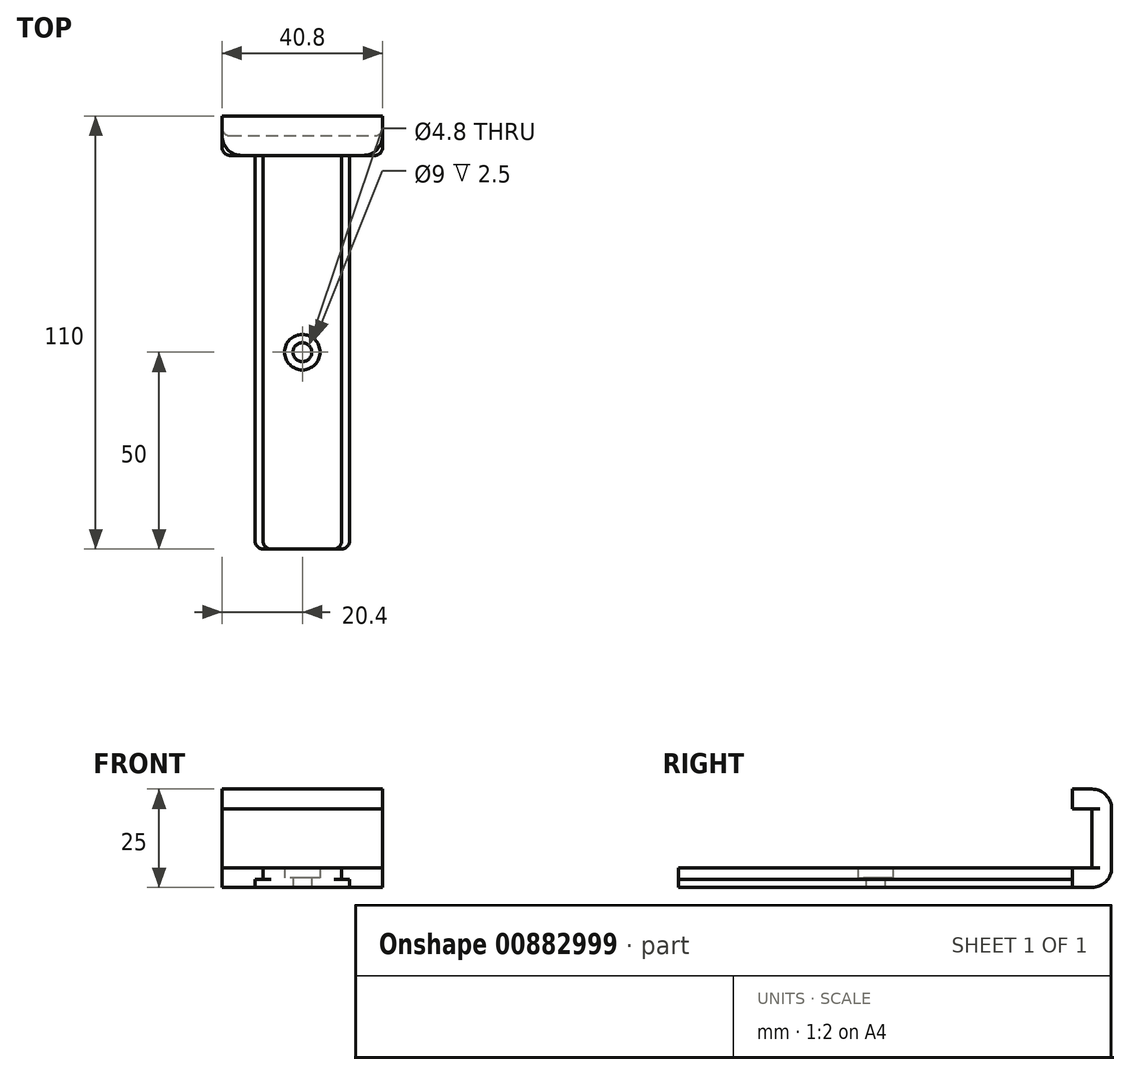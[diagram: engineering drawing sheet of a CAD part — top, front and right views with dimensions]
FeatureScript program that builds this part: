
annotation { "Feature Type Name" : "Feature", "Feature Type Description" : "" }
export const myFeature = defineFeature(function(context is Context, id is Id, definition is map)
    precondition{}
    {
        {
            var Q0;
            Q0=qCreatedBy(makeId("Top.planeOp"),FACE);
            var sketch = newSketch(context, id + "F0", { "sketchPlane" : qUnion([Q0])});
            skLineSegment(sketch, "E0.bottom", {"start": v(10, -50) * mm, "end": v(-10, -50) * mm});
            skLineSegment(sketch, "E0.top", {"start": v(10, 50) * mm, "end": v(-10, 50) * mm});
            skLineSegment(sketch, "E0.left", {"start": v(10, -50) * mm, "end": v(10, 50) * mm});
            skLineSegment(sketch, "E0.right", {"start": v(-10, -50) * mm, "end": v(-10, 50) * mm});
            skPoint(sketch, "E0.middle", {"position": v(0, 0) * mm});
            skLineSegment(sketch, "E1.bottom", {"start": v(-10, -50) * mm, "end": v(-12, -50) * mm});
            skLineSegment(sketch, "E1.top", {"start": v(-10, 50) * mm, "end": v(-12, 50) * mm});
            skLineSegment(sketch, "E1.right", {"start": v(-12, -50) * mm, "end": v(-12, 50) * mm});
            skLineSegment(sketch, "E2.bottom", {"start": v(10, 50) * mm, "end": v(12, 50) * mm});
            skLineSegment(sketch, "E2.top", {"start": v(10, -50) * mm, "end": v(12, -50) * mm});
            skLineSegment(sketch, "E2.left", {"start": v(10, 50) * mm, "end": v(10, -50) * mm});
            skLineSegment(sketch, "E2.right", {"start": v(12, 50) * mm, "end": v(12, -50) * mm});
            skLineSegment(sketch, "E3", {"start": v(0, 50) * mm, "end": v(20.4, 50) * mm});
            skLineSegment(sketch, "E4", {"start": v(20.4, 50) * mm, "end": v(20.4, 60) * mm});
            skLineSegment(sketch, "E5", {"start": v(20.4, 60) * mm, "end": v(-20.4, 60) * mm});
            skLineSegment(sketch, "E6", {"start": v(-20.4, 60) * mm, "end": v(-20.4, 50) * mm});
            skLineSegment(sketch, "E7", {"start": v(-20.4, 50) * mm, "end": v(0, 50) * mm});
            skCircle(sketch, "E8", {"center": v(0, 0) * mm, "radius": 4.5 * mm});
            skCircle(sketch, "E9", {"center": v(0, 0) * mm, "radius": 2.4 * mm});
            skSolve(sketch);
        }
        {
            var Q0;
            Q0=makeQuery(id+"F0.imprint","IMPRINT",FACE,{"disambiguationData":[TD([[makeQuery(id+"F0.imprint","IMPRINT",EDGE,{"derivedFrom":sQuery(id+"F0.wireOp",EDGE,"E8")}),1.0]])]});
            extrude(context, id + "F1", {"entities" : qUnion([Q0]), "depth" : 2.5 * mm, "offsetDistance" : 25 * mm});
        }
        {
            var Q0;
            Q0=makeQuery(id+"F0.imprint","IMPRINT",FACE,{"disambiguationData":[TD([[makeQuery(id+"F0.imprint","IMPRINT",EDGE,{"derivedFrom":sQuery(id+"F0.wireOp",EDGE,"E0.bottom")}),-1.0]])]});
            var Q1;
            {var subQ3=sQuery(id+"F0.wireOp",EDGE,"E1.top");Q1=makeQuery(id+"F0.imprint","IMPRINT",FACE,{"disambiguationData":[TD([[makeQuery(id+"F0.imprint","IMPRINT",EDGE,{"derivedFrom":subQ3}),-1.0]])]});}
            extrude(context, id + "F2", {"entities" : qUnion([Q0, Q1]), "operationType" : NewBodyOperationType.ADD, "depth" : 5 * mm, "offsetDistance" : 25 * mm});
        }
        {
            var Q0;
            Q0=makeQuery(id+"F0.imprint","IMPRINT",FACE,{"disambiguationData":[TD([[makeQuery(id+"F0.imprint","IMPRINT",EDGE,{"derivedFrom":sQuery(id+"F0.wireOp",EDGE,"E0.right")}),1.0]])]});
            var Q1;
            Q1=makeQuery(id+"F0.imprint","IMPRINT",FACE,{"disambiguationData":[TD([[makeQuery(id+"F0.imprint","IMPRINT",EDGE,{"derivedFrom":sQuery(id+"F0.wireOp",EDGE,"E0.left")}),-1.0]])]});
            extrude(context, id + "F3", {"entities" : qUnion([Q0, Q1]), "operationType" : NewBodyOperationType.ADD, "depth" : 2 * mm, "offsetDistance" : 25 * mm});
        }
        {
            var Q0;
            Q0=makeQuery(id+"F2.opExtrude","CAP_FACE",FACE,{"disambiguationData":[OSD([sQuery(id+"F0.wireOp",EDGE,"E0.bottom"),sQuery(id+"F0.wireOp",EDGE,"E0.left"),sQuery(id+"F0.wireOp",EDGE,"E0.right"),sQuery(id+"F0.wireOp",EDGE,"E1.top"),sQuery(id+"F0.wireOp",EDGE,"E2.bottom"),sQuery(id+"F0.wireOp",EDGE,"E3"),sQuery(id+"F0.wireOp",EDGE,"E4"),sQuery(id+"F0.wireOp",EDGE,"E5"),sQuery(id+"F0.wireOp",EDGE,"E6"),sQuery(id+"F0.wireOp",EDGE,"E7"),sQuery(id+"F0.wireOp",EDGE,"E8")])],"isStart":false});
            var sketch = newSketch(context, id + "F4", { "sketchPlane" : qUnion([Q0])});
            skLineSegment(sketch, "E10.bottom", {"start": v(-20.4, 60) * mm, "end": v(20.4, 60) * mm});
            skLineSegment(sketch, "E10.top", {"start": v(-20.4, 55) * mm, "end": v(20.4, 55) * mm});
            skLineSegment(sketch, "E10.left", {"start": v(-20.4, 60) * mm, "end": v(-20.4, 55) * mm});
            skLineSegment(sketch, "E10.right", {"start": v(20.4, 60) * mm, "end": v(20.4, 55) * mm});
            skSolve(sketch);
        }
        {
            var Q0;
            Q0 = qSketchRegion(id + "F4", true);
            extrude(context, id + "F5", {"entities" : qUnion([Q0]), "operationType" : NewBodyOperationType.ADD, "depth" : 15 * mm, "offsetDistance" : 25 * mm});
        }
        {
            var Q0;
            Q0=makeQuery(id+"F5.opExtrude","CAP_FACE",FACE,{"disambiguationData":[OSD([sQuery(id+"F4.wireOp",EDGE,"E10.bottom"),sQuery(id+"F4.wireOp",EDGE,"E10.top"),sQuery(id+"F4.wireOp",EDGE,"E10.left"),sQuery(id+"F4.wireOp",EDGE,"E10.right")])],"isStart":false});
            var sketch = newSketch(context, id + "F6", { "sketchPlane" : qUnion([Q0])});
            skLineSegment(sketch, "E11.bottom", {"start": v(-20.4, 60) * mm, "end": v(20.4, 60) * mm});
            skLineSegment(sketch, "E11.top", {"start": v(-20.4, 50) * mm, "end": v(20.4, 50) * mm});
            skLineSegment(sketch, "E11.left", {"start": v(-20.4, 60) * mm, "end": v(-20.4, 50) * mm});
            skLineSegment(sketch, "E11.right", {"start": v(20.4, 60) * mm, "end": v(20.4, 50) * mm});
            skSolve(sketch);
        }
        {
            var Q0;
            Q0 = qSketchRegion(id + "F6", true);
            extrude(context, id + "F7", {"entities" : qUnion([Q0]), "operationType" : NewBodyOperationType.ADD, "depth" : 5 * mm, "offsetDistance" : 25 * mm});
        }
        {
            var Q0;
            Q0=makeQuery(id+"F7.opExtrude","SWEPT_EDGE",EDGE,{"disambiguationData":[OSD([sQuery(id+"F6.wireOp",EDGE,"E11.top"),sQuery(id+"F6.wireOp",EDGE,"E11.left")])]});
            var Q1;
            Q1=makeQuery(id+"F7.opExtrude","SWEPT_EDGE",EDGE,{"disambiguationData":[OSD([sQuery(id+"F6.wireOp",EDGE,"E11.top"),sQuery(id+"F6.wireOp",EDGE,"E11.right")])]});
            var Q2;
            Q2=makeQuery(id+"F7.opExtrude","CAP_EDGE",EDGE,{"disambiguationData":[OSD([sQuery(id+"F6.wireOp",EDGE,"E11.bottom")])],"isStart":false});
            var Q3;
            Q3=makeQuery(id+"F2.opExtrude","CAP_EDGE",EDGE,{"disambiguationData":[OSD([sQuery(id+"F0.wireOp",EDGE,"E5")])],"isStart":true});
            fillet(context, id + "F8", {"entities" : qUnion([Q0, Q1, Q2, Q3]), "radius" : 5 * mm, "tangentPropagation" : true, "allowEdgeOverflow" : false});
        }
        {
            var Q0;
            Q0=makeQuery(id+"F5.opExtrude","SWEPT_EDGE",EDGE,{"disambiguationData":[OSD([sQuery(id+"F0.wireOp",EDGE,"E6"),sQuery(id+"F4.wireOp",EDGE,"E10.top"),sQuery(id+"F4.wireOp",EDGE,"E10.left")])]});
            var Q1;
            Q1=makeQuery(id+"F5.opExtrude","SWEPT_EDGE",EDGE,{"disambiguationData":[OSD([sQuery(id+"F0.wireOp",EDGE,"E4"),sQuery(id+"F4.wireOp",EDGE,"E10.top"),sQuery(id+"F4.wireOp",EDGE,"E10.right")])]});
            var Q2;
            Q2=makeQuery(id+"F3.opExtrude","SWEPT_EDGE",EDGE,{"disambiguationData":[OSD([sQuery(id+"F0.wireOp",EDGE,"E1.bottom"),sQuery(id+"F0.wireOp",EDGE,"E1.right")])]});
            var Q3;
            Q3=makeQuery(id+"F3.opExtrude","SWEPT_EDGE",EDGE,{"disambiguationData":[OSD([sQuery(id+"F0.wireOp",EDGE,"E2.top"),sQuery(id+"F0.wireOp",EDGE,"E2.right")])]});
            var Q4;
            Q4=makeQuery(id+"F2.opExtrude","SWEPT_EDGE",EDGE,{"disambiguationData":[OSD([sQuery(id+"F0.wireOp",EDGE,"E0.bottom"),sQuery(id+"F0.wireOp",EDGE,"E0.right"),sQuery(id+"F0.wireOp",EDGE,"E1.bottom")])]});
            var Q5;
            Q5=makeQuery(id+"F2.opExtrude","SWEPT_EDGE",EDGE,{"disambiguationData":[OSD([sQuery(id+"F0.wireOp",EDGE,"E0.bottom"),sQuery(id+"F0.wireOp",EDGE,"E0.left"),sQuery(id+"F0.wireOp",EDGE,"E2.top")])]});
            var Q6;
            Q6=makeQuery(id+"F2.opExtrude","SWEPT_EDGE",EDGE,{"disambiguationData":[OSD([sQuery(id+"F0.wireOp",EDGE,"E6"),sQuery(id+"F0.wireOp",EDGE,"E7")])]});
            var Q7;
            Q7=makeQuery(id+"F2.opExtrude","SWEPT_EDGE",EDGE,{"disambiguationData":[OSD([sQuery(id+"F0.wireOp",EDGE,"E3"),sQuery(id+"F0.wireOp",EDGE,"E4")])]});
            fillet(context, id + "F9", {"entities" : qUnion([Q0, Q1, Q2, Q3, Q4, Q5, Q6, Q7]), "radius" : 2 * mm, "tangentPropagation" : true, "allowEdgeOverflow" : false});
        }
    });
